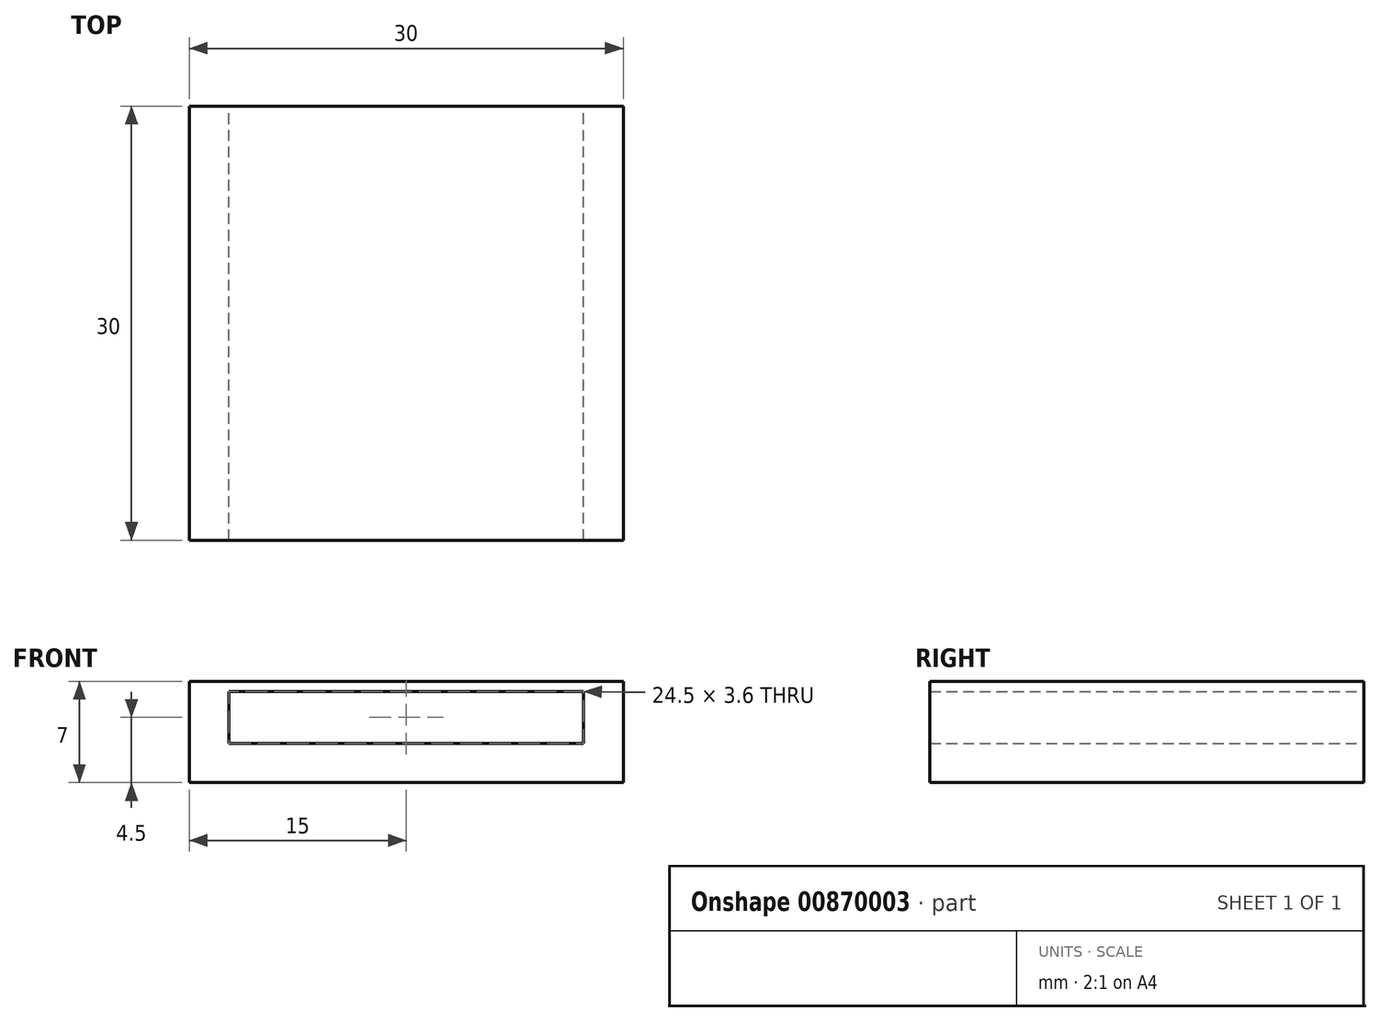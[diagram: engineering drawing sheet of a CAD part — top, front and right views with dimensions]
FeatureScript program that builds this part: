
annotation { "Feature Type Name" : "Feature", "Feature Type Description" : "" }
export const myFeature = defineFeature(function(context is Context, id is Id, definition is map)
    precondition{}
    {
        {
            var Q0;
            Q0=qCreatedBy(makeId("Front.planeOp"),FACE);
            var sketch = newSketch(context, id + "F0", { "sketchPlane" : qUnion([Q0])});
            skLineSegment(sketch, "E0", {"start": v(-15, -3.5) * mm, "end": v(15, -3.5) * mm});
            skLineSegment(sketch, "E1", {"start": v(15, -3.5) * mm, "end": v(15, 3.5) * mm});
            skLineSegment(sketch, "E2", {"start": v(15, 3.5) * mm, "end": v(-15, 3.5) * mm});
            skLineSegment(sketch, "E3", {"start": v(-15, 3.5) * mm, "end": v(-15, -3.5) * mm});
            skLineSegment(sketch, "E4.bottom", {"start": v(-12.25, 2.8) * mm, "end": v(12.25, 2.8) * mm});
            skLineSegment(sketch, "E4.top", {"start": v(-12.25, -0.8) * mm, "end": v(12.25, -0.8) * mm});
            skLineSegment(sketch, "E4.left", {"start": v(-12.25, 2.8) * mm, "end": v(-12.25, -0.8) * mm});
            skLineSegment(sketch, "E4.right", {"start": v(12.25, 2.8) * mm, "end": v(12.25, -0.8) * mm});
            skSolve(sketch);
        }
        {
            var Q0;
            Q0=makeQuery(id+"F0.imprint","IMPRINT",FACE,{"disambiguationData":[TD([[makeQuery(id+"F0.imprint","IMPRINT",EDGE,{"derivedFrom":sQuery(id+"F0.wireOp",EDGE,"E0")}),1.0]])]});
            extrude(context, id + "F1", {"entities" : qUnion([Q0]), "depth" : 30 * mm, "offsetDistance" : 25 * mm});
        }
    });
